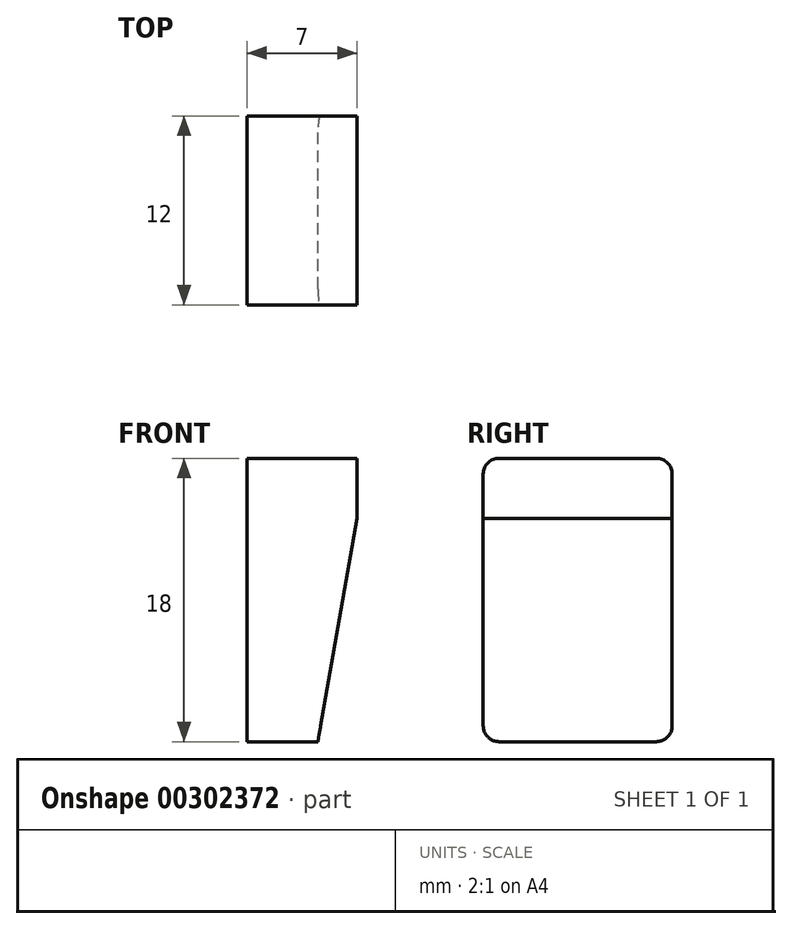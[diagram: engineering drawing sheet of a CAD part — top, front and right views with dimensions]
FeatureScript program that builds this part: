
annotation { "Feature Type Name" : "Feature", "Feature Type Description" : "" }
export const myFeature = defineFeature(function(context is Context, id is Id, definition is map)
    precondition{}
    {
        {
            var Q0;
            Q0=qCreatedBy(makeId("Front.planeOp"),FACE);
            var sketch = newSketch(context, id + "F0", { "sketchPlane" : qUnion([Q0])});
            skLineSegment(sketch, "E0.bottom", {"start": v(0, 0) * mm, "end": v(7, 0) * mm});
            skLineSegment(sketch, "E0.top", {"start": v(0, 18) * mm, "end": v(7, 18) * mm});
            skLineSegment(sketch, "E0.left", {"start": v(0, 0) * mm, "end": v(0, 18) * mm});
            skLineSegment(sketch, "E0.right", {"start": v(7, 0) * mm, "end": v(7, 18) * mm});
            skLineSegment(sketch, "E1", {"start": v(4.5, 0) * mm, "end": v(7, 14.18) * mm});
            skSolve(sketch);
        }
        {
            var Q0;
            {var subQ1=sQuery(id+"F0.wireOp",EDGE,"E0.top");Q0=makeQuery(id+"F0.imprint","IMPRINT",FACE,{"disambiguationData":[TD([[makeQuery(id+"F0.imprint","IMPRINT",EDGE,{"derivedFrom":subQ1}),-1.0]])]});}
            extrude(context, id + "F1", {"entities" : qUnion([Q0]), "endBound" : BoundingType.SYMMETRIC, "depth" : 12 * mm});
        }
        {
            var Q0;
            Q0=makeQuery(id+"F1.opExtrude","CAP_EDGE",EDGE,{"disambiguationData":[OSD([sQuery(id+"F0.wireOp",EDGE,"E0.top")])],"isStart":false});
            var Q1;
            Q1=makeQuery(id+"F1.opExtrude","CAP_EDGE",EDGE,{"disambiguationData":[OSD([sQuery(id+"F0.wireOp",EDGE,"E0.top")])],"isStart":true});
            var Q2;
            Q2=makeQuery(id+"F1.opExtrude","CAP_EDGE",EDGE,{"disambiguationData":[OSD([sQuery(id+"F0.wireOp",EDGE,"E0.bottom")])],"isStart":false});
            var Q3;
            Q3=makeQuery(id+"F1.opExtrude","CAP_EDGE",EDGE,{"disambiguationData":[OSD([sQuery(id+"F0.wireOp",EDGE,"E0.bottom")])],"isStart":true});
            fillet(context, id + "F2", {"entities" : qUnion([Q0, Q1, Q2, Q3]), "radius" : 1 * mm, "tangentPropagation" : true, "allowEdgeOverflow" : false});
        }
    });
